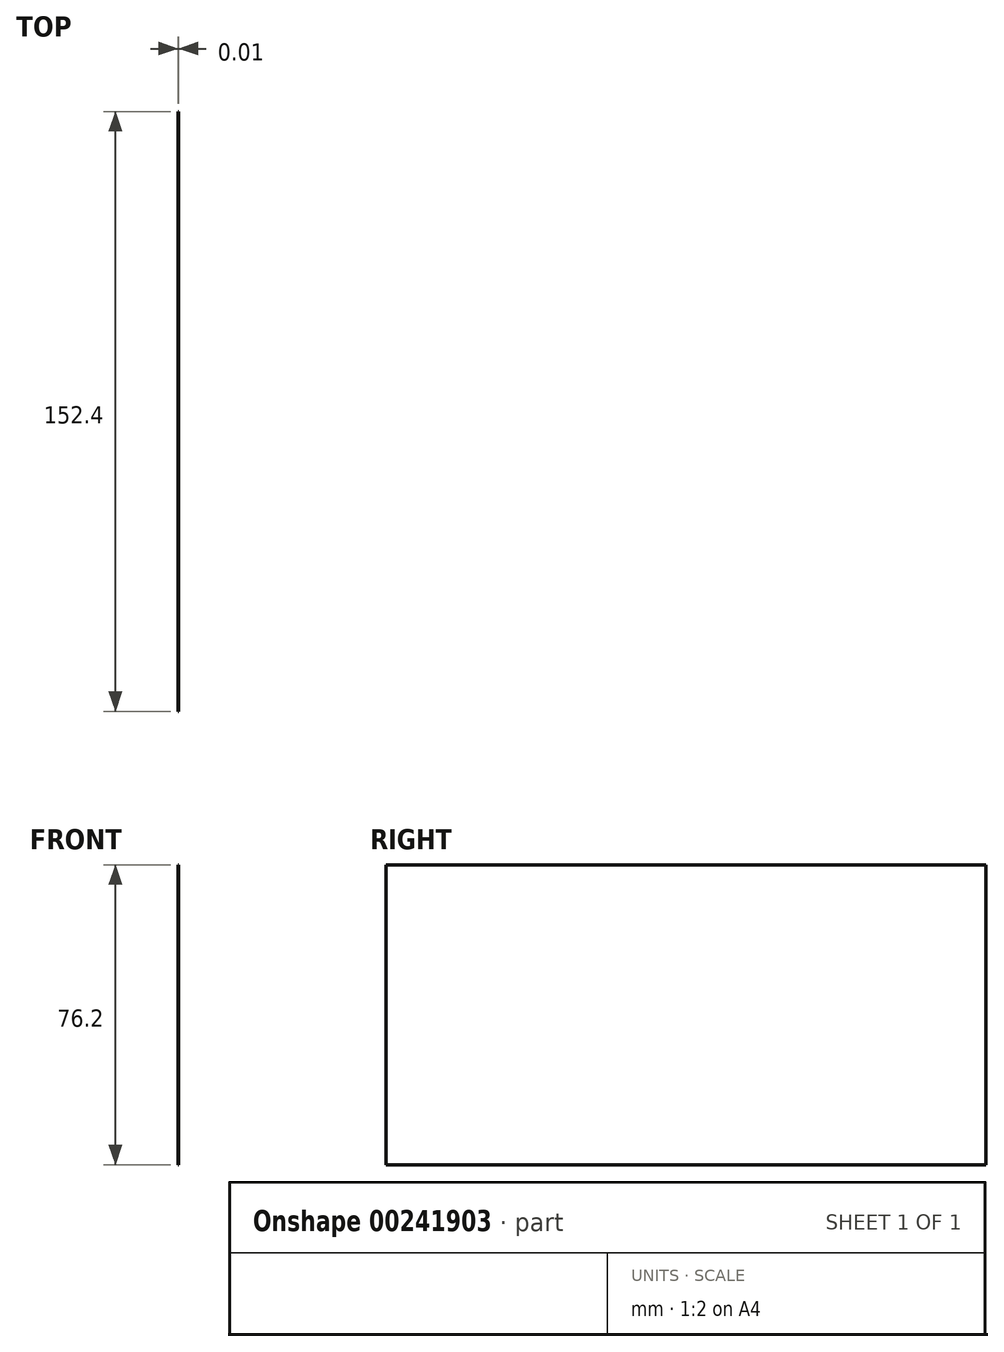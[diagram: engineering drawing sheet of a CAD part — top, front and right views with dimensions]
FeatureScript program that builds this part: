
annotation { "Feature Type Name" : "Feature", "Feature Type Description" : "" }
export const myFeature = defineFeature(function(context is Context, id is Id, definition is map)
    precondition{}
    {
        {
            var Q0;
            Q0=qCreatedBy(makeId("Right.planeOp"),FACE);
            var sketch = newSketch(context, id + "F0", { "sketchPlane" : qUnion([Q0])});
            skLineSegment(sketch, "E0.bottom", {"start": v(-76.2, -38.1) * mm, "end": v(76.2, -38.1) * mm});
            skLineSegment(sketch, "E0.top", {"start": v(-76.2, 38.1) * mm, "end": v(76.2, 38.1) * mm});
            skLineSegment(sketch, "E0.left", {"start": v(-76.2, -38.1) * mm, "end": v(-76.2, 38.1) * mm});
            skLineSegment(sketch, "E0.right", {"start": v(76.2, -38.1) * mm, "end": v(76.2, 38.1) * mm});
            skPoint(sketch, "E0.middle", {"position": v(0, 0) * mm});
            skSolve(sketch);
        }
        {
            var Q0;
            Q0 = qSketchRegion(id + "F0", true);
            extrude(context, id + "F1", {"entities" : qUnion([Q0]), "depth" : 1 / 101.6 * mm});
        }
    });
